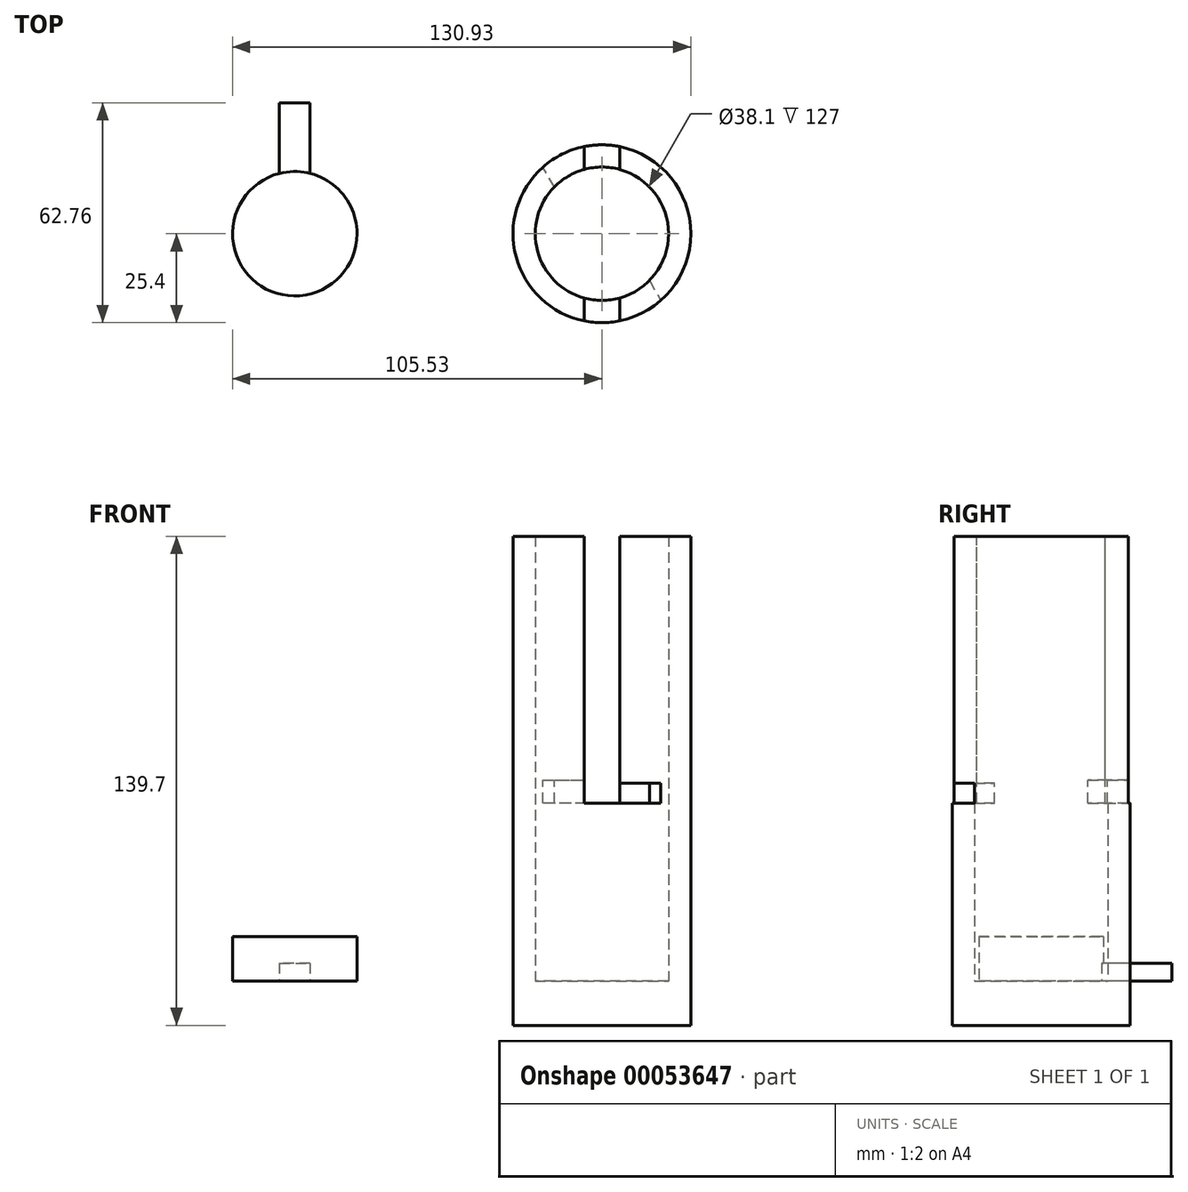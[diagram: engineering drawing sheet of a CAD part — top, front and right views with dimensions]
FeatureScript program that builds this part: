
annotation { "Feature Type Name" : "Feature", "Feature Type Description" : "" }
export const myFeature = defineFeature(function(context is Context, id is Id, definition is map)
    precondition{}
    {
        {
            var Q0;
            Q0=qCreatedBy(makeId("Top.planeOp"),FACE);
            var sketch = newSketch(context, id + "F0", { "sketchPlane" : qUnion([Q0])});
            skCircle(sketch, "E0", {"center": v(0, 0) * mm, "radius": 19.05 * mm});
            skCircle(sketch, "E1.0", {"center": v(0, 0) * mm, "radius": 25.4 * mm});
            skSolve(sketch);
        }
        {
            var Q0;
            Q0=makeQuery(id+"F0.imprint","IMPRINT",FACE,{"disambiguationData":[TD([[makeQuery(id+"F0.imprint","IMPRINT",EDGE,{"derivedFrom":sQuery(id+"F0.wireOp",EDGE,"E0")}),-1.0]])]});
            extrude(context, id + "F1", {"entities" : qUnion([Q0]), "depth" : 127 * mm});
        }
        {
            var Q0;
            Q0=makeQuery(id+"F1.opExtrude","CAP_FACE",FACE,{"disambiguationData":[OSD([sQuery(id+"F0.wireOp",EDGE,"E0"),sQuery(id+"F0.wireOp",EDGE,"E1.0")])],"isStart":false});
            var sketch = newSketch(context, id + "F2", { "sketchPlane" : qUnion([Q0])});
            skLineSegment(sketch, "E2", {"start": v(0, 19.05) * mm, "end": v(0, 25.4) * mm});
            skLineSegment(sketch, "E3", {"start": v(5.08, 18.36) * mm, "end": v(5.08, 24.89) * mm});
            skLineSegment(sketch, "E4.MirrorCS", {"start": v(-5.08, 18.36) * mm, "end": v(-5.08, 24.89) * mm});
            skFitSpline(sketch, "E5", {"points": [v(-5.08, 24.89) * mm, v(0, 25.4) * mm, v(5.08, 24.89) * mm], "startDerivative": vector(10.37, 3.83) * mm, "endDerivative": vector(9.75, -3.38) * mm});
            skFitSpline(sketch, "E6", {"points": [v(5.08, 18.36) * mm, v(0, 19.05) * mm, v(-5.08, 18.36) * mm], "startDerivative": vector(-10.16, 1.23) * mm, "endDerivative": vector(-10.16, -1.23) * mm});
            skLineSegment(sketch, "E7", {"start": v(0, 0) * mm, "end": v(6.97, 0) * mm});
            skLineSegment(sketch, "E8.MirrorCS", {"start": v(0, -19.05) * mm, "end": v(0, -25.4) * mm});
            skLineSegment(sketch, "E9.MirrorCS", {"start": v(5.08, -18.36) * mm, "end": v(5.08, -24.89) * mm});
            skLineSegment(sketch, "E10.MirrorCS", {"start": v(-5.08, -18.36) * mm, "end": v(-5.08, -24.89) * mm});
            skFitSpline(sketch, "E11", {"points": [v(-5.08, -18.36) * mm, v(0, -18.36) * mm, v(5.08, -18.36) * mm], "startDerivative": vector(10.16, 0) * mm, "endDerivative": vector(10.16, 0) * mm});
            skFitSpline(sketch, "E12", {"points": [v(-5.08, -24.89) * mm, v(-2.57, -26.08) * mm, v(3, -26.44) * mm, v(5.08, -24.89) * mm], "startDerivative": vector(7, -4.35) * mm, "endDerivative": vector(5.65, 6.63) * mm});
            skSolve(sketch);
        }
        {
            var Q0;
            {var subQ0=sQuery(id+"F2.wireOp",EDGE,"E2");Q0=makeQuery(id+"F2.imprint","IMPRINT",FACE,{"disambiguationData":[TD([[makeQuery(id+"F2.imprint","IMPRINT",EDGE,{"derivedFrom":subQ0}),1.0]])]});}
            var Q1;
            {var subQ0=sQuery(id+"F2.wireOp",EDGE,"E2");Q1=makeQuery(id+"F2.imprint","IMPRINT",FACE,{"disambiguationData":[TD([[makeQuery(id+"F2.imprint","IMPRINT",EDGE,{"derivedFrom":subQ0}),-1.0]])]});}
            extrude(context, id + "F3", {"entities" : qUnion([Q0, Q1]), "operationType" : NewBodyOperationType.REMOVE, "oppositeDirection" : true, "depth" : 76.2 * mm});
        }
        {
            var Q0;
            Q0=makeQuery(id+"F1.opExtrude","CAP_FACE",FACE,{"disambiguationData":[OSD([sQuery(id+"F0.wireOp",EDGE,"E0"),sQuery(id+"F0.wireOp",EDGE,"E1.0")])],"isStart":true});
            var sketch = newSketch(context, id + "F4", { "sketchPlane" : qUnion([Q0])});
            skCircle(sketch, "E13", {"center": v(0, 0) * mm, "radius": 25.4 * mm});
            skSolve(sketch);
        }
        {
            var Q0;
            Q0 = qSketchRegion(id + "F4", true);
            extrude(context, id + "F5", {"entities" : qUnion([Q0]), "operationType" : NewBodyOperationType.ADD, "depth" : 12.7 * mm});
        }
        {
            var Q0;
            Q0=makeQuery(id+"F3.boolean.opBoolean","COPY",FACE,{"derivedFrom":makeQuery(id+"F3.opExtrude","SWEPT_FACE",FACE,{"disambiguationData":[OSD([sQuery(id+"F2.wireOp",EDGE,"E4.MirrorCS")])]})});
            var sketch = newSketch(context, id + "F6", { "sketchPlane" : qUnion([Q0])});
            skLineSegment(sketch, "E14.bottom", {"start": v(24.89, 50.8) * mm, "end": v(18.36, 50.8) * mm});
            skLineSegment(sketch, "E14.top", {"start": v(24.89, 57.34) * mm, "end": v(18.36, 57.34) * mm});
            skLineSegment(sketch, "E14.left", {"start": v(24.89, 50.8) * mm, "end": v(24.89, 57.34) * mm});
            skLineSegment(sketch, "E14.right", {"start": v(18.36, 50.8) * mm, "end": v(18.36, 57.34) * mm});
            skSolve(sketch);
        }
        {
            var Q0;
            Q0 = qSketchRegion(id + "F6", true);
            var Q1;
            Q1=makeQuery(id+"F1.opExtrude","SWEPT_FACE",FACE,{"disambiguationData":[OSD([sQuery(id+"F0.wireOp",EDGE,"E0")])]});
            revolve(context, id + "F7", {"operationType" : NewBodyOperationType.REMOVE, "entities" : qUnion([Q0]), "axis" : qUnion([Q1]), "revolveType" : RevolveType.ONE_DIRECTION, "angle" : 30 * degree});
        }
        {
            var Q0;
            Q0=qCreatedBy(makeId("Top.planeOp"),FACE);
            var sketch = newSketch(context, id + "F8", { "sketchPlane" : qUnion([Q0])});
            skCircle(sketch, "E15", {"center": v(-87.75, 0) * mm, "radius": 17.78 * mm});
            skLineSegment(sketch, "E16", {"start": v(-87.75, 37.36) * mm, "end": v(-83.39, 37.36) * mm});
            skLineSegment(sketch, "E17", {"start": v(-92.12, 37.36) * mm, "end": v(-87.75, 37.36) * mm});
            skLineSegment(sketch, "E18", {"start": v(-87.75, 37.36) * mm, "end": v(-87.75, 17.78) * mm});
            skLineSegment(sketch, "E19", {"start": v(-83.39, 37.36) * mm, "end": v(-83.39, 17.24) * mm});
            skLineSegment(sketch, "E20.MirrorCS", {"start": v(-92.12, 37.36) * mm, "end": v(-92.12, 17.24) * mm});
            skSolve(sketch);
        }
        {
            var Q0;
            {var subQ0=sQuery(id+"F8.wireOp",EDGE,"E15");var subQ1=makeQuery(id+"F8.imprint","INTERSECT",VERTEX,{"derivedFrom":[subQ0,sQuery(id+"F8.wireOp",EDGE,"E18")]});Q0=makeQuery(id+"F8.imprint","IMPRINT",FACE,{"disambiguationData":[TD([[makeQuery(id+"F8.imprint","IMPRINT",EDGE,{"disambiguationData":[TD([[subQ1,1.0]])],"derivedFrom":subQ0}),1.0]])]});}
            extrude(context, id + "F9", {"entities" : qUnion([Q0]), "depth" : 12.7 * mm});
        }
        {
            var Q0;
            Q0=makeQuery(id+"F8.imprint","IMPRINT",FACE,{"disambiguationData":[TD([[makeQuery(id+"F8.imprint","IMPRINT",EDGE,{"derivedFrom":sQuery(id+"F8.wireOp",EDGE,"E17")}),-1.0]])]});
            var Q1;
            Q1=makeQuery(id+"F8.imprint","IMPRINT",FACE,{"disambiguationData":[TD([[makeQuery(id+"F8.imprint","IMPRINT",EDGE,{"derivedFrom":sQuery(id+"F8.wireOp",EDGE,"E16")}),-1.0]])]});
            extrude(context, id + "F10", {"entities" : qUnion([Q0, Q1]), "operationType" : NewBodyOperationType.ADD, "depth" : 5.08 * mm});
        }
        {
            var Q0;
            {var subQ0=sQuery(id+"F2.wireOp",EDGE,"E8.MirrorCS");Q0=makeQuery(id+"F2.imprint","IMPRINT",FACE,{"disambiguationData":[TD([[makeQuery(id+"F2.imprint","IMPRINT",EDGE,{"derivedFrom":subQ0}),-1.0]])]});}
            var Q1;
            {var subQ0=sQuery(id+"F2.wireOp",EDGE,"E8.MirrorCS");Q1=makeQuery(id+"F2.imprint","IMPRINT",FACE,{"disambiguationData":[TD([[makeQuery(id+"F2.imprint","IMPRINT",EDGE,{"derivedFrom":subQ0}),1.0]])]});}
            extrude(context, id + "F11", {"entities" : qUnion([Q0, Q1]), "operationType" : NewBodyOperationType.REMOVE, "oppositeDirection" : true, "depth" : 76.2 * mm});
        }
        {
            var Q0;
            Q0=makeQuery(id+"F11.boolean.opBoolean","COPY",FACE,{"derivedFrom":makeQuery(id+"F11.opExtrude","SWEPT_FACE",FACE,{"disambiguationData":[OSD([sQuery(id+"F2.wireOp",EDGE,"E9.MirrorCS")])]})});
            var sketch = newSketch(context, id + "F12", { "sketchPlane" : qUnion([Q0])});
            skLineSegment(sketch, "E21.bottom", {"start": v(18.36, 50.8) * mm, "end": v(24.89, 50.8) * mm});
            skLineSegment(sketch, "E21.top", {"start": v(18.36, 50.8) * mm, "end": v(24.89, 50.8) * mm});
            skLineSegment(sketch, "E21.left", {"start": v(18.36, 50.8) * mm, "end": v(18.36, 50.8) * mm});
            skLineSegment(sketch, "E21.right", {"start": v(24.89, 50.8) * mm, "end": v(24.89, 50.8) * mm});
            skLineSegment(sketch, "E22.bottom", {"start": v(24.89, 50.8) * mm, "end": v(18.36, 50.8) * mm});
            skLineSegment(sketch, "E22.top", {"start": v(24.89, 56.52) * mm, "end": v(18.36, 56.52) * mm});
            skLineSegment(sketch, "E22.left", {"start": v(24.89, 50.8) * mm, "end": v(24.89, 56.52) * mm});
            skLineSegment(sketch, "E22.right", {"start": v(18.36, 50.8) * mm, "end": v(18.36, 56.52) * mm});
            skSolve(sketch);
        }
        {
            var Q0;
            Q0 = qSketchRegion(id + "F12", true);
            var Q1;
            Q1=makeQuery(id+"F1.opExtrude","SWEPT_FACE",FACE,{"disambiguationData":[OSD([sQuery(id+"F0.wireOp",EDGE,"E0")])]});
            revolve(context, id + "F13", {"operationType" : NewBodyOperationType.REMOVE, "entities" : qUnion([Q0]), "axis" : qUnion([Q1]), "revolveType" : RevolveType.ONE_DIRECTION, "angle" : 30 * degree});
        }
    });
